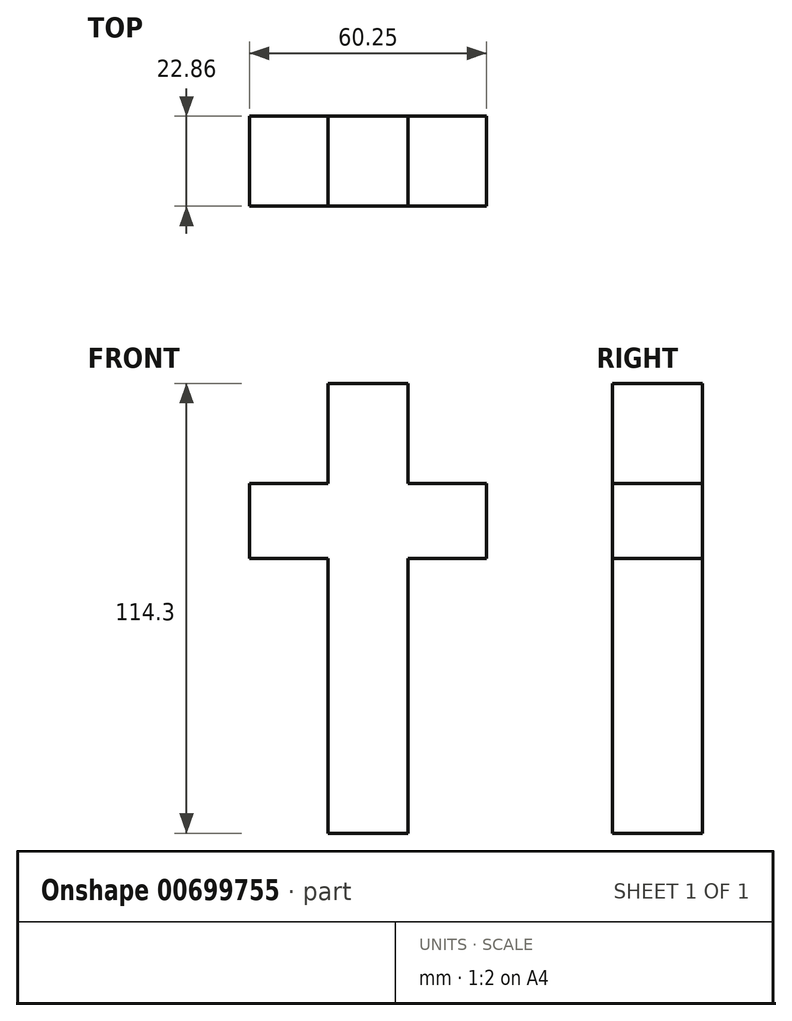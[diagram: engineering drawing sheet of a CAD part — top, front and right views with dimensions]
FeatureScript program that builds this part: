
annotation { "Feature Type Name" : "Feature", "Feature Type Description" : "" }
export const myFeature = defineFeature(function(context is Context, id is Id, definition is map)
    precondition{}
    {
        {
            var Q0;
            Q0=qCreatedBy(makeId("Front.planeOp"),FACE);
            var sketch = newSketch(context, id + "F0", { "sketchPlane" : qUnion([Q0])});
            skLineSegment(sketch, "E0", {"start": v(-9.67, -44) * mm, "end": v(10.65, -44) * mm});
            skLineSegment(sketch, "E1", {"start": v(10.65, -44) * mm, "end": v(10.65, 25.84) * mm});
            skLineSegment(sketch, "E2", {"start": v(10.65, 25.84) * mm, "end": v(30.6, 25.84) * mm});
            skLineSegment(sketch, "E3", {"start": v(30.6, 25.84) * mm, "end": v(30.6, 44.9) * mm});
            skLineSegment(sketch, "E4", {"start": v(30.6, 44.9) * mm, "end": v(10.65, 44.9) * mm});
            skLineSegment(sketch, "E5", {"start": v(10.65, 44.9) * mm, "end": v(10.65, 70.3) * mm});
            skLineSegment(sketch, "E6", {"start": v(10.65, 70.3) * mm, "end": v(-9.67, 70.3) * mm});
            skLineSegment(sketch, "E7", {"start": v(-9.67, 70.3) * mm, "end": v(-9.67, 44.9) * mm});
            skLineSegment(sketch, "E8", {"start": v(-9.67, 44.9) * mm, "end": v(-29.64, 44.9) * mm});
            skLineSegment(sketch, "E9", {"start": v(-29.64, 44.9) * mm, "end": v(-29.64, 25.84) * mm});
            skLineSegment(sketch, "E10", {"start": v(-29.64, 25.84) * mm, "end": v(-9.67, 25.84) * mm});
            skLineSegment(sketch, "E11", {"start": v(-9.67, 25.84) * mm, "end": v(-9.67, -44) * mm});
            skSolve(sketch);
        }
        {
            var Q0;
            Q0 = qSketchRegion(id + "F0", true);
            extrude(context, id + "F1", {"entities" : qUnion([Q0]), "depth" : 22.86 * mm, "offsetDistance" : 25.4 * mm});
        }
    });
